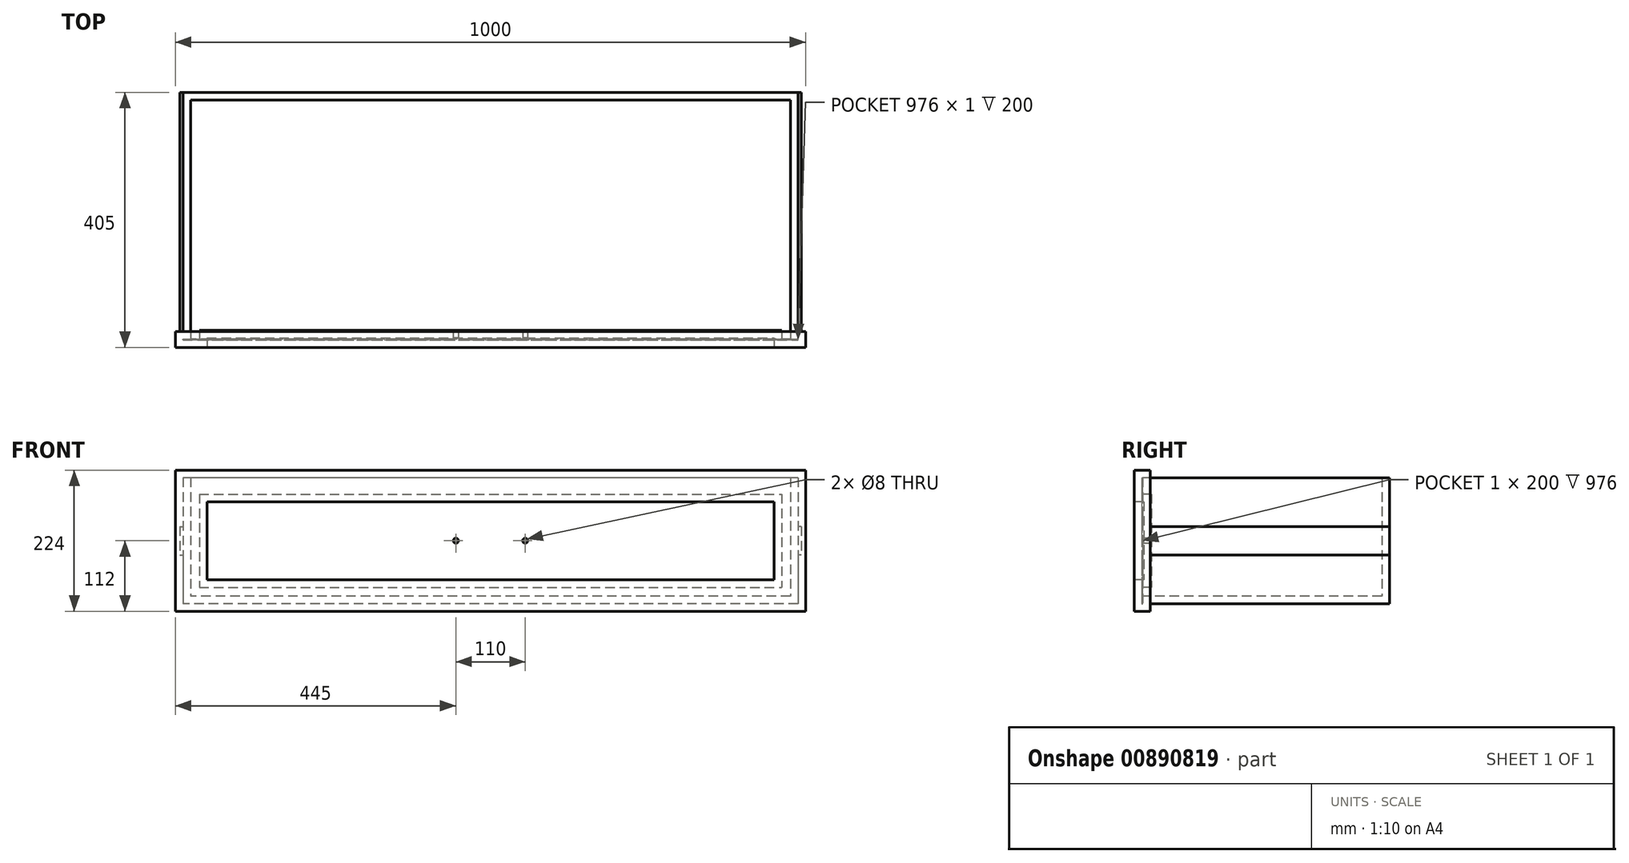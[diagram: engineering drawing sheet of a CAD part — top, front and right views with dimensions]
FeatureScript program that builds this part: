
annotation { "Feature Type Name" : "Feature", "Feature Type Description" : "" }
export const myFeature = defineFeature(function(context is Context, id is Id, definition is map)
    precondition{}
    {
        {
            var Q0;
            Q0=qCreatedBy(makeId("Front.planeOp"),FACE);
            var sketch = newSketch(context, id + "F0", { "sketchPlane" : qUnion([Q0])});
            skLineSegment(sketch, "E0.bottom", {"start": v(-500, 106.47) * mm, "end": v(500, 106.47) * mm});
            skLineSegment(sketch, "E0.top", {"start": v(-500, -106.47) * mm, "end": v(500, -106.47) * mm});
            skLineSegment(sketch, "E0.left", {"start": v(-500, 106.47) * mm, "end": v(-500, -106.47) * mm});
            skLineSegment(sketch, "E0.right", {"start": v(500, 106.47) * mm, "end": v(500, -106.47) * mm});
            skPoint(sketch, "E0.middle", {"position": v(0, 0) * mm});
            skLineSegment(sketch, "E1.bottom", {"start": v(-500, 112) * mm, "end": v(500, 112) * mm});
            skLineSegment(sketch, "E1.top", {"start": v(-500, -112) * mm, "end": v(500, -112) * mm});
            skLineSegment(sketch, "E1.left", {"start": v(-500, 112) * mm, "end": v(-500, -112) * mm});
            skLineSegment(sketch, "E1.right", {"start": v(500, 112) * mm, "end": v(500, -112) * mm});
            skSolve(sketch);
        }
        {
            var Q0;
            Q0 = qSketchRegion(id + "F0", true);
            extrude(context, id + "F1", {"entities" : qUnion([Q0]), "depth" : 25 * mm, "offsetDistance" : 25 * mm});
        }
        {
            var Q0;
            Q0=makeQuery(id+"F1.opExtrude","CAP_FACE",FACE,{"disambiguationData":[OSD([sQuery(id+"F0.wireOp",EDGE,"E1.bottom"),sQuery(id+"F0.wireOp",EDGE,"E1.top"),sQuery(id+"F0.wireOp",EDGE,"E1.left"),sQuery(id+"F0.wireOp",EDGE,"E1.right")])],"isStart":false});
            var sketch = newSketch(context, id + "F2", { "sketchPlane" : qUnion([Q0])});
            skLineSegment(sketch, "E2.bottom", {"start": v(-450, 62) * mm, "end": v(450, 62) * mm});
            skLineSegment(sketch, "E2.top", {"start": v(-450, -62) * mm, "end": v(450, -62) * mm});
            skLineSegment(sketch, "E2.left", {"start": v(-450, 62) * mm, "end": v(-450, -62) * mm});
            skLineSegment(sketch, "E2.right", {"start": v(450, 62) * mm, "end": v(450, -62) * mm});
            skPoint(sketch, "E2.middle", {"position": v(0, 0) * mm});
            skSolve(sketch);
        }
        {
            var Q0;
            Q0 = qSketchRegion(id + "F2", true);
            extrude(context, id + "F3", {"entities" : qUnion([Q0]), "operationType" : NewBodyOperationType.REMOVE, "oppositeDirection" : true, "depth" : 15 * mm, "offsetDistance" : 25 * mm});
        }
        {
            var Q0;
            Q0=makeQuery(id+"F1.opExtrude","CAP_FACE",FACE,{"disambiguationData":[OSD([sQuery(id+"F0.wireOp",EDGE,"E1.bottom"),sQuery(id+"F0.wireOp",EDGE,"E1.top"),sQuery(id+"F0.wireOp",EDGE,"E1.left"),sQuery(id+"F0.wireOp",EDGE,"E1.right")])],"isStart":true});
            var sketch = newSketch(context, id + "F4", { "sketchPlane" : qUnion([Q0])});
            skLineSegment(sketch, "E3.bottom", {"start": v(-488, 100) * mm, "end": v(488, 100) * mm});
            skLineSegment(sketch, "E3.top", {"start": v(-488, -100) * mm, "end": v(488, -100) * mm});
            skLineSegment(sketch, "E3.left", {"start": v(-488, 100) * mm, "end": v(-488, -100) * mm});
            skLineSegment(sketch, "E3.right", {"start": v(488, 100) * mm, "end": v(488, -100) * mm});
            skPoint(sketch, "E3.middle", {"position": v(0, 0) * mm});
            skSolve(sketch);
        }
        {
            var Q0;
            Q0 = qSketchRegion(id + "F4", true);
            extrude(context, id + "F5", {"entities" : qUnion([Q0]), "operationType" : NewBodyOperationType.ADD, "depth" : 380 * mm, "offsetDistance" : 25 * mm});
        }
        {
            var Q0;
            Q0=makeQuery(id+"F5.opExtrude","SWEPT_FACE",FACE,{"disambiguationData":[OSD([sQuery(id+"F4.wireOp",EDGE,"E3.bottom")])]});
            shell(context, id + "F6", {"entities" : qUnion([Q0]), "thickness" : 12 * mm});
        }
        {
            var Q0;
            Q0=makeQuery(id+"F5.opExtrude","SWEPT_FACE",FACE,{"disambiguationData":[OSD([sQuery(id+"F4.wireOp",EDGE,"E3.right")])]});
            var sketch = newSketch(context, id + "F7", { "sketchPlane" : qUnion([Q0])});
            skLineSegment(sketch, "E4", {"start": v(0, 0) * mm, "end": v(-380, 0) * mm, "construction": true});
            skPoint(sketch, "E5.middle", {"position": v(-190, 0) * mm});
            skLineSegment(sketch, "E6.bottom", {"start": v(-380, 22.5) * mm, "end": v(0, 22.5) * mm});
            skLineSegment(sketch, "E6.top", {"start": v(-380, -22.5) * mm, "end": v(0, -22.5) * mm});
            skLineSegment(sketch, "E6.left", {"start": v(-380, 22.5) * mm, "end": v(-380, -22.5) * mm});
            skLineSegment(sketch, "E6.right", {"start": v(0, 22.5) * mm, "end": v(0, -22.5) * mm});
            skSolve(sketch);
        }
        {
            var Q0;
            Q0 = qSketchRegion(id + "F7", true);
            extrude(context, id + "F8", {"entities" : qUnion([Q0]), "operationType" : NewBodyOperationType.ADD, "depth" : 5 * mm, "offsetDistance" : 25 * mm});
        }
        {
            var Q0;
            Q0=makeQuery(id+"F5.opExtrude","SWEPT_FACE",FACE,{"disambiguationData":[OSD([sQuery(id+"F4.wireOp",EDGE,"E3.left")])]});
            var sketch = newSketch(context, id + "F9", { "sketchPlane" : qUnion([Q0])});
            skLineSegment(sketch, "E7", {"start": v(0, 0) * mm, "end": v(380, 0) * mm, "construction": true});
            skLineSegment(sketch, "E8.bottom", {"start": v(0, 22.5) * mm, "end": v(380, 22.5) * mm});
            skLineSegment(sketch, "E8.top", {"start": v(0, -22.5) * mm, "end": v(380, -22.5) * mm});
            skLineSegment(sketch, "E8.left", {"start": v(0, 22.5) * mm, "end": v(0, -22.5) * mm});
            skLineSegment(sketch, "E8.right", {"start": v(380, 22.5) * mm, "end": v(380, -22.5) * mm});
            skPoint(sketch, "E8.middle", {"position": v(190, 0) * mm});
            skSolve(sketch);
        }
        {
            var Q0;
            Q0 = qSketchRegion(id + "F9", true);
            extrude(context, id + "F10", {"entities" : qUnion([Q0]), "operationType" : NewBodyOperationType.ADD, "depth" : 5 * mm, "offsetDistance" : 25 * mm});
        }
        {
            var Q0;
            Q0=makeQuery(id+"F3.boolean.opBoolean","COPY",FACE,{"derivedFrom":makeQuery(id+"F3.opExtrude","CAP_FACE",FACE,{"disambiguationData":[OSD([sQuery(id+"F2.wireOp",EDGE,"E2.bottom"),sQuery(id+"F2.wireOp",EDGE,"E2.top"),sQuery(id+"F2.wireOp",EDGE,"E2.left"),sQuery(id+"F2.wireOp",EDGE,"E2.right")])],"isStart":false})});
            var sketch = newSketch(context, id + "F11", { "sketchPlane" : qUnion([Q0])});
            skLineSegment(sketch, "E9", {"start": v(0, 0) * mm, "end": v(-55, 0) * mm});
            skLineSegment(sketch, "E10", {"start": v(0, 0) * mm, "end": v(55, 0) * mm});
            skCircle(sketch, "E11", {"center": v(-55, 0) * mm, "radius": 4 * mm});
            skCircle(sketch, "E12", {"center": v(55, 0) * mm, "radius": 4 * mm});
            skSolve(sketch);
        }
        {
            var Q0;
            Q0 = qSketchRegion(id + "F11", true);
            extrude(context, id + "F12", {"entities" : qUnion([Q0]), "operationType" : NewBodyOperationType.REMOVE, "endBound" : BoundingType.UP_TO_NEXT, "oppositeDirection" : true, "depth" : 25 * mm, "offsetDistance" : 25 * mm});
        }
    });
